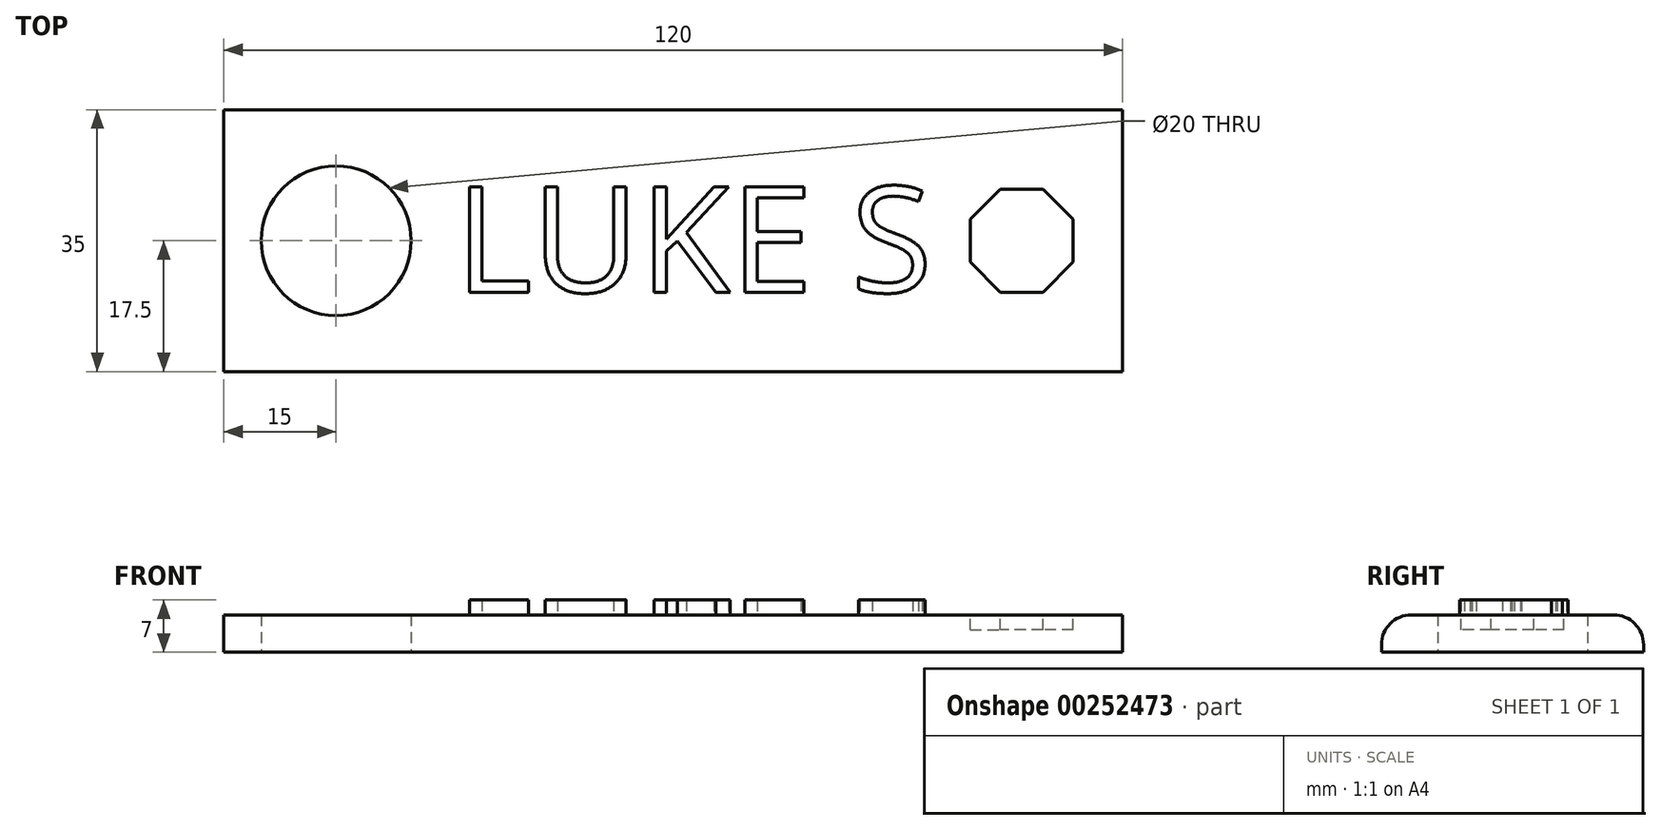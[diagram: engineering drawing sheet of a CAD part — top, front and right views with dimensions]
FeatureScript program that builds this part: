
annotation { "Feature Type Name" : "Feature", "Feature Type Description" : "" }
export const myFeature = defineFeature(function(context is Context, id is Id, definition is map)
    precondition{}
    {
        {
            var Q0;
            Q0=qCreatedBy(makeId("Top.planeOp"),FACE);
            var sketch = newSketch(context, id + "F0", { "sketchPlane" : qUnion([Q0])});
            skLineSegment(sketch, "E0.bottom", {"start": v(60, 17.5) * mm, "end": v(-60, 17.5) * mm});
            skLineSegment(sketch, "E0.top", {"start": v(60, -17.5) * mm, "end": v(-60, -17.5) * mm});
            skLineSegment(sketch, "E0.left", {"start": v(60, 17.5) * mm, "end": v(60, -17.5) * mm});
            skLineSegment(sketch, "E0.right", {"start": v(-60, 17.5) * mm, "end": v(-60, -17.5) * mm});
            skPoint(sketch, "E0.middle", {"position": v(0, 0) * mm});
            skCircle(sketch, "E1", {"center": v(-45, 0) * mm, "radius": 10 * mm});
            skPoint(sketch, "E1.centerSnap0", {"position": v(-60, 0) * mm});
            skSolve(sketch);
        }
        {
            var Q0;
            Q0=makeQuery(id+"F0.imprint","IMPRINT",FACE,{"disambiguationData":[TD([[makeQuery(id+"F0.imprint","IMPRINT",EDGE,{"derivedFrom":sQuery(id+"F0.wireOp",EDGE,"E0.bottom")}),1.0]])]});
            extrude(context, id + "F1", {"entities" : qUnion([Q0]), "depth" : 5 * mm});
        }
        {
            var Q0;
            Q0=makeQuery(id+"F1.opExtrude","CAP_EDGE",EDGE,{"disambiguationData":[OSD([sQuery(id+"F0.wireOp",EDGE,"E0.top")])],"isStart":false});
            fillet(context, id + "F2", {"entities" : qUnion([Q0]), "radius" : 4 * mm, "tangentPropagation" : true, "allowEdgeOverflow" : false});
        }
        {
            var Q0;
            Q0=makeQuery(id+"F1.opExtrude","CAP_EDGE",EDGE,{"disambiguationData":[OSD([sQuery(id+"F0.wireOp",EDGE,"E0.bottom")])],"isStart":false});
            fillet(context, id + "F3", {"entities" : qUnion([Q0]), "radius" : 4 * mm, "tangentPropagation" : true, "allowEdgeOverflow" : false});
        }
        {
            var Q0;
            Q0=makeQuery(id+"F1.opExtrude","CAP_FACE",FACE,{"disambiguationData":[OSD([sQuery(id+"F0.wireOp",EDGE,"E0.bottom"),sQuery(id+"F0.wireOp",EDGE,"E0.top"),sQuery(id+"F0.wireOp",EDGE,"E0.left"),sQuery(id+"F0.wireOp",EDGE,"E0.right"),sQuery(id+"F0.wireOp",EDGE,"E1")])],"isStart":false});
            var sketch = newSketch(context, id + "F4", { "sketchPlane" : qUnion([Q0])});
            skText(sketch, "E2", { "text": "LUKE S", "fontName": "OpenSans-Regular.ttf"});
            const initialGuessF4  = {"E2": [-0.02912, -0.00688, 1, 0, 0.01422]};
            skSetInitialGuess(sketch, initialGuessF4);
            skSolve(sketch);
        }
        {
            var Q0;
            Q0=makeQuery(id+"F4.imprint","IMPRINT",FACE,{"disambiguationData":[TD([[makeQuery(id+"F4.imprint","IMPRINT",EDGE,{"derivedFrom":sQuery(id+"F4.wireOp",EDGE,"E2.sketch_text.stroke-0")}),1.0]])]});
            var sketch = newSketch(context, id + "F5", { "sketchPlane" : qUnion([Q0])});
            skCircle(sketch, "E3.cCircle", {"center": v(46.55, 0) * mm, "radius": 6.88 * mm, "construction": true});
            skLineSegment(sketch, "E3.0", {"start": v(49.4, -6.88) * mm, "end": v(43.7, -6.88) * mm});
            skLineSegment(sketch, "E3.1", {"start": v(43.7, -6.88) * mm, "end": v(39.67, -2.85) * mm});
            skLineSegment(sketch, "E3.2", {"start": v(39.67, -2.85) * mm, "end": v(39.67, 2.85) * mm});
            skLineSegment(sketch, "E3.3", {"start": v(39.67, 2.85) * mm, "end": v(43.7, 6.88) * mm});
            skLineSegment(sketch, "E3.4", {"start": v(43.7, 6.88) * mm, "end": v(49.4, 6.88) * mm});
            skLineSegment(sketch, "E3.5", {"start": v(49.4, 6.88) * mm, "end": v(53.43, 2.85) * mm});
            skLineSegment(sketch, "E3.6", {"start": v(53.43, 2.85) * mm, "end": v(53.43, -2.85) * mm});
            skLineSegment(sketch, "E3.7", {"start": v(53.43, -2.85) * mm, "end": v(49.4, -6.88) * mm});
            skPoint(sketch, "E3.0.midPoint", {"position": v(46.55, -6.88) * mm});
            skSolve(sketch);
        }
        {
            var Q0;
            Q0 = qSketchRegion(id + "F4", true);
            extrude(context, id + "F6", {"entities" : qUnion([Q0]), "operationType" : NewBodyOperationType.ADD, "depth" : 2 * mm});
        }
        {
            var Q0;
            Q0=makeQuery(id+"F5.imprint","IMPRINT",FACE,{"disambiguationData":[TD([[makeQuery(id+"F5.imprint","IMPRINT",EDGE,{"derivedFrom":sQuery(id+"F5.wireOp",EDGE,"E3.0")}),-1.0]])]});
            extrude(context, id + "F7", {"entities" : qUnion([Q0]), "operationType" : NewBodyOperationType.REMOVE, "oppositeDirection" : true, "depth" : 2 * mm});
        }
    });
